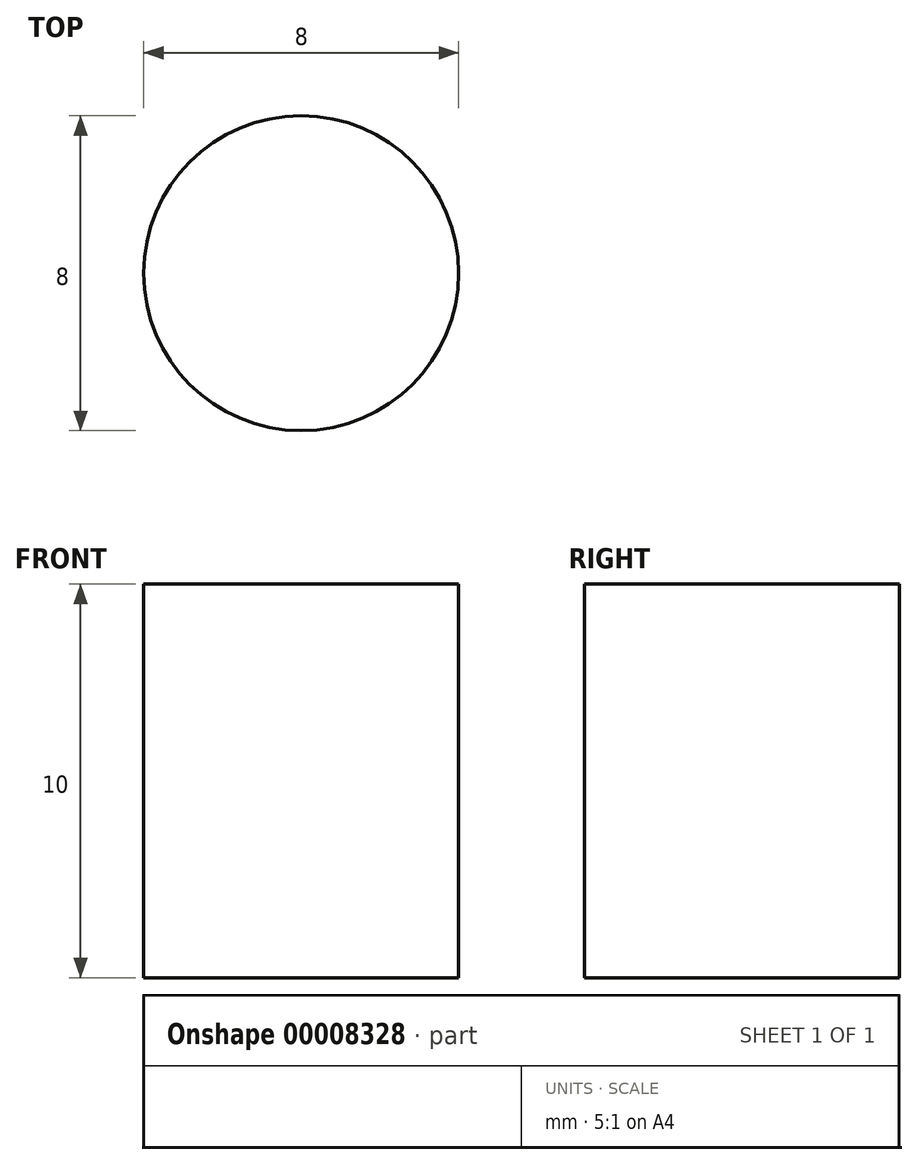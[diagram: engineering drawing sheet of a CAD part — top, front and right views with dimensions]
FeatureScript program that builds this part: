
annotation { "Feature Type Name" : "Feature", "Feature Type Description" : "" }
export const myFeature = defineFeature(function(context is Context, id is Id, definition is map)
    precondition{}
    {
        {
            var Q0;
            Q0=qCreatedBy(makeId("Top.planeOp"),FACE);
            var sketch = newSketch(context, id + "F0", { "sketchPlane" : qUnion([Q0])});
            skCircle(sketch, "E0", {"center": v(0, 0) * mm, "radius": 4 * mm});
            skSolve(sketch);
        }
        {
            var Q0;
            Q0=makeQuery(id+"F0.imprint","IMPRINT",FACE,{"disambiguationData":[TD([[makeQuery(id+"F0.imprint","IMPRINT",EDGE,{"derivedFrom":sQuery(id+"F0.wireOp",EDGE,"E0")}),1.0]])]});
            extrude(context, id + "F1", {"entities" : qUnion([Q0]), "depth" : 10 * mm});
        }
    });
